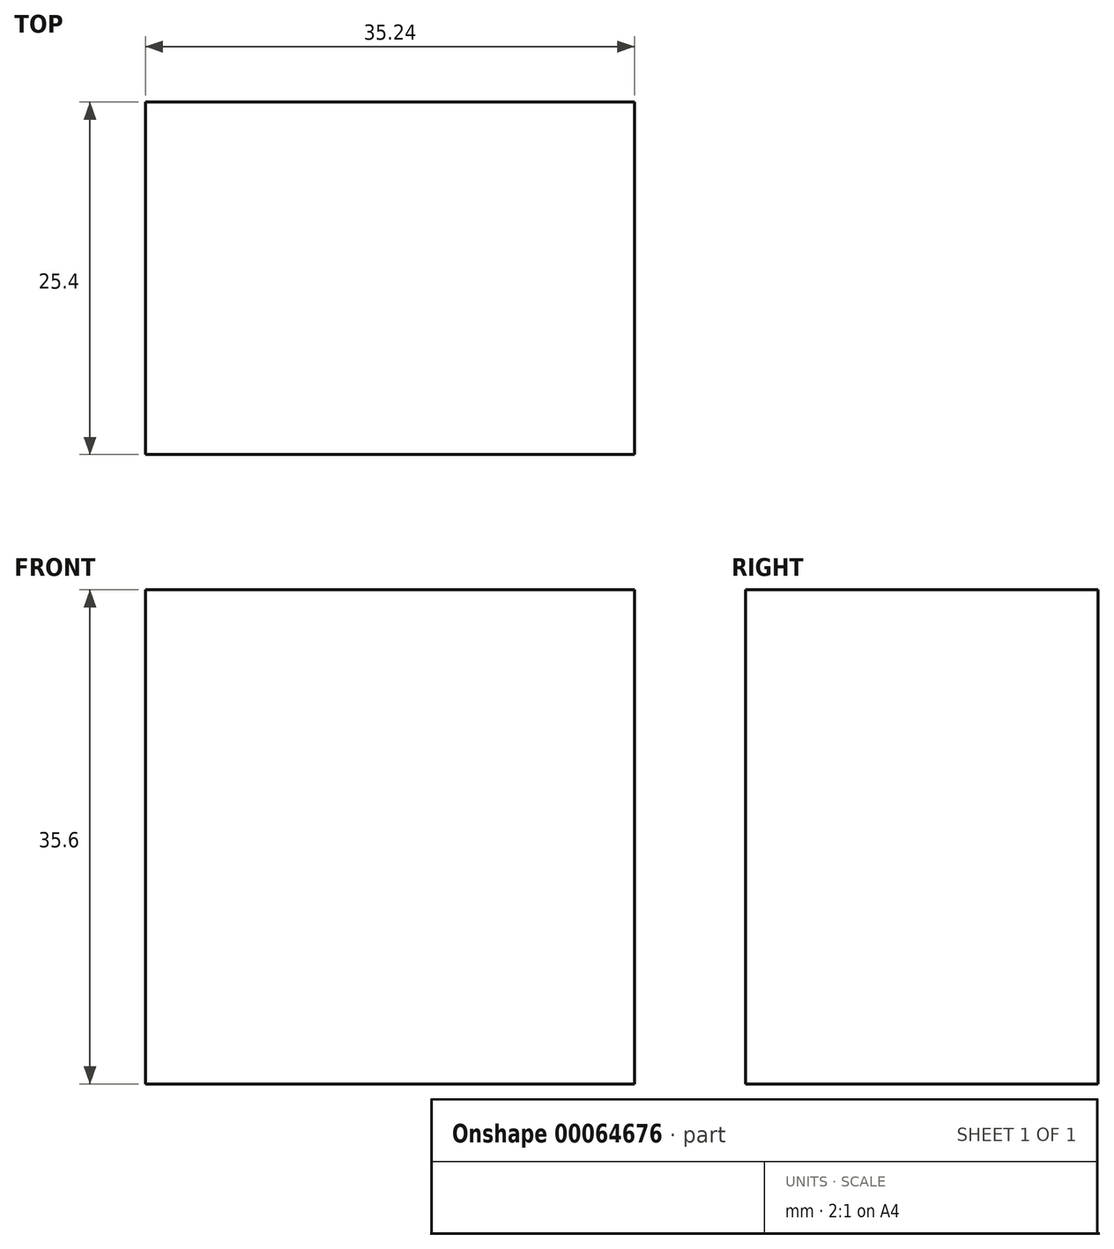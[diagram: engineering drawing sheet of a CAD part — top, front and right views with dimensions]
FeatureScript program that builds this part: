
annotation { "Feature Type Name" : "Feature", "Feature Type Description" : "" }
export const myFeature = defineFeature(function(context is Context, id is Id, definition is map)
    precondition{}
    {
        {
            var Q0;
            Q0=qCreatedBy(makeId("Front.planeOp"),FACE);
            var sketch = newSketch(context, id + "F0", { "sketchPlane" : qUnion([Q0])});
            skLineSegment(sketch, "E0.bottom", {"start": v(0, 0) * mm, "end": v(35.24, 0) * mm});
            skLineSegment(sketch, "E0.top", {"start": v(0, 35.6) * mm, "end": v(35.24, 35.6) * mm});
            skLineSegment(sketch, "E0.left", {"start": v(0, 0) * mm, "end": v(0, 35.6) * mm});
            skLineSegment(sketch, "E0.right", {"start": v(35.24, 0) * mm, "end": v(35.24, 35.6) * mm});
            skSolve(sketch);
        }
        {
            var Q0;
            Q0 = qSketchRegion(id + "F0", true);
            extrude(context, id + "F1", {"entities" : qUnion([Q0]), "depth" : 25.4 * mm});
        }
    });
